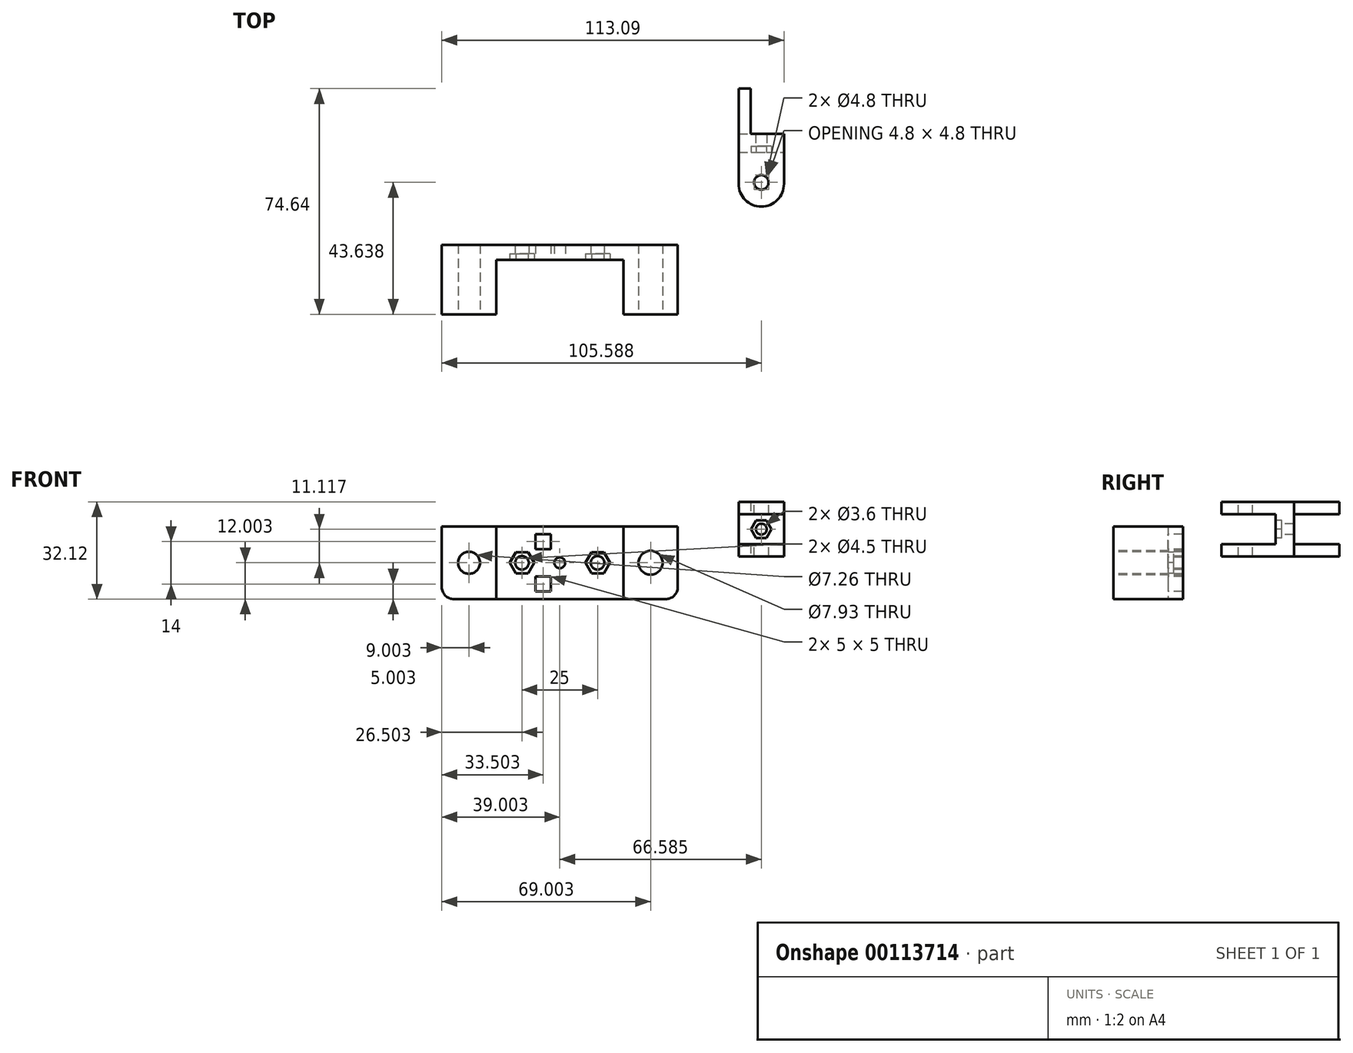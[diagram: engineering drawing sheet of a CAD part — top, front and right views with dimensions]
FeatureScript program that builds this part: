
annotation { "Feature Type Name" : "Feature", "Feature Type Description" : "" }
export const myFeature = defineFeature(function(context is Context, id is Id, definition is map)
    precondition{}
    {
        {
            var Q0;
            Q0=qCreatedBy(makeId("Front.planeOp"),FACE);
            var sketch = newSketch(context, id + "F0", { "sketchPlane" : qUnion([Q0])});
            skLineSegment(sketch, "E0", {"start": v(-49.77, -14.12) * mm, "end": v(-49.77, 9.88) * mm});
            skLineSegment(sketch, "E1", {"start": v(28.23, 9.88) * mm, "end": v(28.23, -14.12) * mm});
            skLineSegment(sketch, "E2", {"start": v(28.23, -14.12) * mm, "end": v(-49.77, -14.12) * mm});
            skLineSegment(sketch, "E3", {"start": v(-49.77, 9.88) * mm, "end": v(28.23, 9.88) * mm});
            skSolve(sketch);
        }
        {
            var Q0;
            Q0=makeQuery(id+"F0.imprint","IMPRINT",FACE,{"disambiguationData":[TD([[makeQuery(id+"F0.imprint","IMPRINT",EDGE,{"derivedFrom":sQuery(id+"F0.wireOp",EDGE,"E0")}),-1.0]])]});
            extrude(context, id + "F1", {"entities" : qUnion([Q0]), "depth" : 5 * mm});
        }
        {
            var Q0;
            Q0=makeQuery(id+"F1.opExtrude","CAP_FACE",FACE,{"disambiguationData":[OSD([sQuery(id+"F0.wireOp",EDGE,"E0"),sQuery(id+"F0.wireOp",EDGE,"pnh9ggrm-5665-z1nB-cMV6-CIKma8F3alFQ"),sQuery(id+"F0.wireOp",EDGE,"BvfvvXhj-ewnM-89mg-FvGF-KvGd08tOQLcB"),sQuery(id+"F0.wireOp",EDGE,"7k9m0oyc-eC8G-DHzC-QoAq-Q04KNSwf5TuD"),sQuery(id+"F0.wireOp",EDGE,"E1"),sQuery(id+"F0.wireOp",EDGE,"E2")])],"isStart":false});
            var sketch = newSketch(context, id + "F2", { "sketchPlane" : qUnion([Q0])});
            skCircle(sketch, "E4", {"center": v(-23.27, -2.12) * mm, "radius": 2.25 * mm});
            skCircle(sketch, "E5", {"center": v(1.73, -2.12) * mm, "radius": 2.25 * mm});
            skLineSegment(sketch, "E6", {"start": v(-49.77, -2.12) * mm, "end": v(28.23, -2.12) * mm, "construction": true});
            skCircle(sketch, "E7.cCircle", {"center": v(-23.27, -2.12) * mm, "radius": 3.5 * mm, "construction": true});
            skLineSegment(sketch, "E7.0", {"start": v(-25.29, 1.38) * mm, "end": v(-21.25, 1.38) * mm});
            skLineSegment(sketch, "E7.1", {"start": v(-21.25, 1.38) * mm, "end": v(-19.23, -2.12) * mm});
            skLineSegment(sketch, "E7.2", {"start": v(-19.23, -2.12) * mm, "end": v(-21.25, -5.62) * mm});
            skLineSegment(sketch, "E7.3", {"start": v(-21.25, -5.62) * mm, "end": v(-25.29, -5.62) * mm});
            skLineSegment(sketch, "E7.4", {"start": v(-25.29, -5.62) * mm, "end": v(-27.3, -2.12) * mm});
            skLineSegment(sketch, "E7.5", {"start": v(-27.3, -2.12) * mm, "end": v(-25.29, 1.38) * mm});
            skPoint(sketch, "E7.0.midPoint", {"position": v(-23.27, 1.38) * mm});
            skCircle(sketch, "E8.cCircle", {"center": v(1.73, -2.12) * mm, "radius": 3.5 * mm, "construction": true});
            skLineSegment(sketch, "E8.0", {"start": v(-0.29, 1.38) * mm, "end": v(3.75, 1.38) * mm});
            skLineSegment(sketch, "E8.1", {"start": v(3.75, 1.38) * mm, "end": v(5.77, -2.12) * mm});
            skLineSegment(sketch, "E8.2", {"start": v(5.77, -2.12) * mm, "end": v(3.75, -5.62) * mm});
            skLineSegment(sketch, "E8.3", {"start": v(3.75, -5.62) * mm, "end": v(-0.29, -5.62) * mm});
            skLineSegment(sketch, "E8.4", {"start": v(-0.29, -5.62) * mm, "end": v(-2.3, -2.12) * mm});
            skLineSegment(sketch, "E8.5", {"start": v(-2.3, -2.12) * mm, "end": v(-0.29, 1.38) * mm});
            skPoint(sketch, "E8.0.midPoint", {"position": v(1.73, 1.38) * mm});
            skCircle(sketch, "E9", {"center": v(-10.77, -2.12) * mm, "radius": 1.8 * mm});
            skLineSegment(sketch, "E10", {"start": v(-10.77, 9.88) * mm, "end": v(-10.77, -14.12) * mm, "construction": true});
            skSolve(sketch);
        }
        {
            var Q0;
            Q0=makeQuery(id+"F2.imprint","IMPRINT",FACE,{"disambiguationData":[TD([[makeQuery(id+"F2.imprint","IMPRINT",EDGE,{"derivedFrom":sQuery(id+"F2.wireOp",EDGE,"E4")}),1.0]])]});
            var Q1;
            Q1=makeQuery(id+"F2.imprint","IMPRINT",FACE,{"disambiguationData":[TD([[makeQuery(id+"F2.imprint","IMPRINT",EDGE,{"derivedFrom":sQuery(id+"F2.wireOp",EDGE,"E5")}),1.0]])]});
            extrude(context, id + "F3", {"entities" : qUnion([Q0, Q1]), "operationType" : NewBodyOperationType.REMOVE, "oppositeDirection" : true, "depth" : 25 * mm});
        }
        {
            var Q0;
            Q0=makeQuery(id+"F2.imprint","IMPRINT",FACE,{"disambiguationData":[TD([[makeQuery(id+"F2.imprint","IMPRINT",EDGE,{"derivedFrom":sQuery(id+"F2.wireOp",EDGE,"E4")}),-1.0]])]});
            var Q1;
            Q1=makeQuery(id+"F2.imprint","IMPRINT",FACE,{"disambiguationData":[TD([[makeQuery(id+"F2.imprint","IMPRINT",EDGE,{"derivedFrom":sQuery(id+"F2.wireOp",EDGE,"E5")}),-1.0]])]});
            extrude(context, id + "F4", {"entities" : qUnion([Q0, Q1]), "operationType" : NewBodyOperationType.REMOVE, "oppositeDirection" : true, "depth" : 2 * mm});
        }
        {
            var Q0;
            Q0=makeQuery(id+"F2.imprint","IMPRINT",FACE,{"disambiguationData":[TD([[makeQuery(id+"F2.imprint","IMPRINT",EDGE,{"derivedFrom":sQuery(id+"F2.wireOp",EDGE,"E7.0")}),1.0]])]});
            var sketch = newSketch(context, id + "F5", { "sketchPlane" : qUnion([Q0])});
            skLineSegment(sketch, "E11.bottom", {"start": v(-18.77, -6.62) * mm, "end": v(-13.77, -6.62) * mm});
            skLineSegment(sketch, "E11.top", {"start": v(-18.77, -11.62) * mm, "end": v(-13.77, -11.62) * mm});
            skLineSegment(sketch, "E11.left", {"start": v(-18.77, -6.62) * mm, "end": v(-18.77, -11.62) * mm});
            skLineSegment(sketch, "E11.right", {"start": v(-13.77, -6.62) * mm, "end": v(-13.77, -11.62) * mm});
            skLineSegment(sketch, "E12.bottom", {"start": v(-18.77, 2.38) * mm, "end": v(-13.77, 2.38) * mm});
            skLineSegment(sketch, "E12.top", {"start": v(-18.77, 7.38) * mm, "end": v(-13.77, 7.38) * mm});
            skLineSegment(sketch, "E12.left", {"start": v(-18.77, 2.38) * mm, "end": v(-18.77, 7.38) * mm});
            skLineSegment(sketch, "E12.right", {"start": v(-13.77, 2.38) * mm, "end": v(-13.77, 7.38) * mm});
            skLineSegment(sketch, "E13", {"start": v(-10.77, -14.12) * mm, "end": v(-10.77, 9.88) * mm, "construction": true});
            skSolve(sketch);
        }
        {
            var Q0;
            Q0=makeQuery(id+"F5.imprint","IMPRINT",FACE,{"disambiguationData":[TD([[makeQuery(id+"F5.imprint","IMPRINT",EDGE,{"derivedFrom":sQuery(id+"F5.wireOp",EDGE,"E11.bottom")}),-1.0]])]});
            var Q1;
            Q1=makeQuery(id+"F5.imprint","IMPRINT",FACE,{"disambiguationData":[TD([[makeQuery(id+"F5.imprint","IMPRINT",EDGE,{"derivedFrom":sQuery(id+"F5.wireOp",EDGE,"E12.bottom")}),1.0]])]});
            extrude(context, id + "F6", {"entities" : qUnion([Q0, Q1]), "operationType" : NewBodyOperationType.REMOVE, "oppositeDirection" : true, "depth" : 25 * mm});
        }
        {
            var Q0;
            Q0=makeQuery(id+"F1.opExtrude","CAP_FACE",FACE,{"disambiguationData":[OSD([sQuery(id+"F0.wireOp",EDGE,"E0"),sQuery(id+"F0.wireOp",EDGE,"pnh9ggrm-5665-z1nB-cMV6-CIKma8F3alFQ"),sQuery(id+"F0.wireOp",EDGE,"BvfvvXhj-ewnM-89mg-FvGF-KvGd08tOQLcB"),sQuery(id+"F0.wireOp",EDGE,"7k9m0oyc-eC8G-DHzC-QoAq-Q04KNSwf5TuD"),sQuery(id+"F0.wireOp",EDGE,"E1"),sQuery(id+"F0.wireOp",EDGE,"E2")])],"isStart":false});
            var sketch = newSketch(context, id + "F7", { "sketchPlane" : qUnion([Q0])});
            skLineSegment(sketch, "E14.bottom", {"start": v(28.23, 9.88) * mm, "end": v(10.23, 9.88) * mm});
            skLineSegment(sketch, "E14.top", {"start": v(28.23, -14.12) * mm, "end": v(10.23, -14.12) * mm});
            skLineSegment(sketch, "E14.left", {"start": v(28.23, 9.88) * mm, "end": v(28.23, -14.12) * mm});
            skLineSegment(sketch, "E14.right", {"start": v(10.23, 9.88) * mm, "end": v(10.23, -14.12) * mm});
            skLineSegment(sketch, "E15.bottom", {"start": v(-49.77, 9.88) * mm, "end": v(-31.77, 9.88) * mm});
            skLineSegment(sketch, "E15.top", {"start": v(-49.77, -14.12) * mm, "end": v(-31.77, -14.12) * mm});
            skLineSegment(sketch, "E15.left", {"start": v(-49.77, 9.88) * mm, "end": v(-49.77, -14.12) * mm});
            skLineSegment(sketch, "E15.right", {"start": v(-31.77, 9.88) * mm, "end": v(-31.77, -14.12) * mm});
            skSolve(sketch);
        }
        {
            var Q0;
            Q0=makeQuery(id+"F7.imprint","IMPRINT",FACE,{"disambiguationData":[TD([[makeQuery(id+"F7.imprint","IMPRINT",EDGE,{"derivedFrom":sQuery(id+"F7.wireOp",EDGE,"E15.bottom")}),-1.0]])]});
            var Q1;
            Q1=makeQuery(id+"F7.imprint","IMPRINT",FACE,{"disambiguationData":[TD([[makeQuery(id+"F7.imprint","IMPRINT",EDGE,{"derivedFrom":sQuery(id+"F7.wireOp",EDGE,"E14.bottom")}),-1.0]])]});
            extrude(context, id + "F8", {"entities" : qUnion([Q0, Q1]), "operationType" : NewBodyOperationType.ADD, "depth" : 18 * mm});
        }
        {
            var Q0;
            Q0=makeQuery(id+"F2.imprint","IMPRINT",FACE,{"disambiguationData":[TD([[makeQuery(id+"F2.imprint","IMPRINT",EDGE,{"derivedFrom":sQuery(id+"F2.wireOp",EDGE,"E7.0")}),1.0]])]});
            var sketch = newSketch(context, id + "F9", { "sketchPlane" : qUnion([Q0])});
            skCircle(sketch, "E16", {"center": v(-40.77, -2.12) * mm, "radius": 3.63 * mm});
            skCircle(sketch, "E17", {"center": v(19.23, -2.12) * mm, "radius": 3.96 * mm});
            skLineSegment(sketch, "E18", {"start": v(-49.77, -2.12) * mm, "end": v(28.23, -2.12) * mm, "construction": true});
            skSolve(sketch);
        }
        {
            var Q0;
            Q0=makeQuery(id+"F9.imprint","IMPRINT",FACE,{"disambiguationData":[TD([[makeQuery(id+"F9.imprint","IMPRINT",EDGE,{"derivedFrom":sQuery(id+"F9.wireOp",EDGE,"E16")}),1.0]])]});
            var Q1;
            Q1=makeQuery(id+"F9.imprint","IMPRINT",FACE,{"disambiguationData":[TD([[makeQuery(id+"F9.imprint","IMPRINT",EDGE,{"derivedFrom":sQuery(id+"F9.wireOp",EDGE,"E17")}),1.0]])]});
            extrude(context, id + "F10", {"entities" : qUnion([Q0, Q1]), "operationType" : NewBodyOperationType.REMOVE, "endBound" : BoundingType.SYMMETRIC, "oppositeDirection" : true, "depth" : 60 * mm});
        }
        {
            var Q0;
            Q0=makeQuery(id+"F8.boolean.opBoolean","MERGE",EDGE,{"derivedFrom":[makeQuery(id+"F1.opExtrude","SWEPT_EDGE",EDGE,{"disambiguationData":[OSD([sQuery(id+"F0.wireOp",EDGE,"E0"),sQuery(id+"F0.wireOp",EDGE,"E2")])]}),makeQuery(id+"F8.opExtrude","SWEPT_EDGE",EDGE,{"disambiguationData":[OSD([sQuery(id+"F7.wireOp",EDGE,"7sFVJVFp-NuRY-99qe-KacD-1ADUzF3ini2G.top"),sQuery(id+"F7.wireOp",EDGE,"7sFVJVFp-NuRY-99qe-KacD-1ADUzF3ini2G.left")])]})]});
            var Q1;
            Q1=makeQuery(id+"F8.boolean.opBoolean","MERGE",EDGE,{"derivedFrom":[makeQuery(id+"F1.opExtrude","SWEPT_EDGE",EDGE,{"disambiguationData":[OSD([sQuery(id+"F0.wireOp",EDGE,"E1"),sQuery(id+"F0.wireOp",EDGE,"E2")])]}),makeQuery(id+"F8.opExtrude","SWEPT_EDGE",EDGE,{"disambiguationData":[OSD([sQuery(id+"F7.wireOp",EDGE,"E14.top"),sQuery(id+"F7.wireOp",EDGE,"E14.left")])]})]});
            fillet(context, id + "F11", {"entities" : qUnion([Q0, Q1]), "radius" : 4 * mm, "tangentPropagation" : true, "allowEdgeOverflow" : false});
        }
        {
            var Q0;
            Q0=makeQuery(id+"F2.imprint","IMPRINT",FACE,{"disambiguationData":[TD([[makeQuery(id+"F2.imprint","IMPRINT",EDGE,{"derivedFrom":sQuery(id+"F2.wireOp",EDGE,"E9")}),1.0]])]});
            extrude(context, id + "F12", {"entities" : qUnion([Q0]), "operationType" : NewBodyOperationType.REMOVE, "oppositeDirection" : true, "depth" : 25 * mm});
        }
        {
            var Q0;
            Q0=qCreatedBy(makeId("Top.planeOp"),FACE);
            var sketch = newSketch(context, id + "F13", { "sketchPlane" : qUnion([Q0])});
            skLineSegment(sketch, "E19", {"start": v(48.32, 51.64) * mm, "end": v(52.32, 51.64) * mm});
            skLineSegment(sketch, "E20", {"start": v(52.32, 51.64) * mm, "end": v(52.32, 36.64) * mm});
            skLineSegment(sketch, "E21", {"start": v(52.32, 36.64) * mm, "end": v(63.32, 36.64) * mm});
            skLineSegment(sketch, "E22", {"start": v(63.32, 36.64) * mm, "end": v(63.32, 12.64) * mm});
            skLineSegment(sketch, "E23", {"start": v(63.32, 12.64) * mm, "end": v(48.32, 12.64) * mm});
            skLineSegment(sketch, "E24", {"start": v(48.32, 12.64) * mm, "end": v(48.32, 51.64) * mm});
            skSolve(sketch);
        }
        {
            var Q0;
            Q0=makeQuery(id+"F13.imprint","IMPRINT",FACE,{"disambiguationData":[TD([[makeQuery(id+"F13.imprint","IMPRINT",EDGE,{"derivedFrom":sQuery(id+"F13.wireOp",EDGE,"E19")}),-1.0]])]});
            extrude(context, id + "F14", {"entities" : qUnion([Q0]), "depth" : 18 * mm});
        }
        {
            var Q0;
            Q0=makeQuery(id+"F14.opExtrude","SWEPT_FACE",FACE,{"disambiguationData":[OSD([sQuery(id+"F13.wireOp",EDGE,"E20")])]});
            var sketch = newSketch(context, id + "F15", { "sketchPlane" : qUnion([Q0])});
            skLineSegment(sketch, "E25.bottom", {"start": v(51.64, 14) * mm, "end": v(36.64, 14) * mm});
            skLineSegment(sketch, "E25.top", {"start": v(51.64, 4) * mm, "end": v(36.64, 4) * mm});
            skLineSegment(sketch, "E25.left", {"start": v(51.64, 14) * mm, "end": v(51.64, 4) * mm});
            skLineSegment(sketch, "E25.right", {"start": v(36.64, 14) * mm, "end": v(36.64, 4) * mm});
            skSolve(sketch);
        }
        {
            var Q0;
            Q0=makeQuery(id+"F15.imprint","IMPRINT",FACE,{"disambiguationData":[TD([[makeQuery(id+"F15.imprint","IMPRINT",EDGE,{"derivedFrom":sQuery(id+"F15.wireOp",EDGE,"E25.bottom")}),1.0]])]});
            extrude(context, id + "F16", {"entities" : qUnion([Q0]), "operationType" : NewBodyOperationType.REMOVE, "oppositeDirection" : true, "depth" : 25 * mm});
        }
        {
            var Q0;
            Q0=makeQuery(id+"F14.opExtrude","SWEPT_FACE",FACE,{"disambiguationData":[OSD([sQuery(id+"F13.wireOp",EDGE,"E22")])]});
            var sketch = newSketch(context, id + "F17", { "sketchPlane" : qUnion([Q0])});
            skLineSegment(sketch, "E26.bottom", {"start": v(12.64, 14) * mm, "end": v(30.64, 14) * mm});
            skLineSegment(sketch, "E26.top", {"start": v(12.64, 4) * mm, "end": v(30.64, 4) * mm});
            skLineSegment(sketch, "E26.left", {"start": v(12.64, 14) * mm, "end": v(12.64, 4) * mm});
            skLineSegment(sketch, "E26.right", {"start": v(30.64, 14) * mm, "end": v(30.64, 4) * mm});
            skSolve(sketch);
        }
        {
            var Q0;
            Q0=makeQuery(id+"F17.imprint","IMPRINT",FACE,{"disambiguationData":[TD([[makeQuery(id+"F17.imprint","IMPRINT",EDGE,{"derivedFrom":sQuery(id+"F17.wireOp",EDGE,"E26.bottom")}),-1.0]])]});
            extrude(context, id + "F18", {"entities" : qUnion([Q0]), "operationType" : NewBodyOperationType.REMOVE, "oppositeDirection" : true, "depth" : 25 * mm});
        }
        {
            var Q0;
            Q0=makeQuery(id+"F14.opExtrude","CAP_FACE",FACE,{"disambiguationData":[OSD([sQuery(id+"F13.wireOp",EDGE,"E19"),sQuery(id+"F13.wireOp",EDGE,"E20"),sQuery(id+"F13.wireOp",EDGE,"E21"),sQuery(id+"F13.wireOp",EDGE,"E22"),sQuery(id+"F13.wireOp",EDGE,"E23"),sQuery(id+"F13.wireOp",EDGE,"E24")])],"isStart":false});
            var sketch = newSketch(context, id + "F19", { "sketchPlane" : qUnion([Q0])});
            skCircle(sketch, "E27", {"center": v(55.82, 20.64) * mm, "radius": 2.4 * mm});
            skSolve(sketch);
        }
        {
            var Q0;
            Q0=makeQuery(id+"F19.imprint","IMPRINT",FACE,{"disambiguationData":[TD([[makeQuery(id+"F19.imprint","IMPRINT",EDGE,{"derivedFrom":sQuery(id+"F19.wireOp",EDGE,"E27")}),1.0]])]});
            extrude(context, id + "F20", {"entities" : qUnion([Q0]), "operationType" : NewBodyOperationType.REMOVE, "oppositeDirection" : true, "depth" : 25 * mm});
        }
        {
            var Q0;
            {var subQ0=sQuery(id+"F13.wireOp",EDGE,"E24");var subQ1=sQuery(id+"F13.wireOp",EDGE,"E23");Q0=makeQuery(id+"F18.boolean.opBoolean","SPLIT",EDGE,{"disambiguationData":[TD([makeQuery(id+"F18.opExtrude","SWEPT_FACE",FACE,{"disambiguationData":[OSD([sQuery(id+"F17.wireOp",EDGE,"E26.bottom")])]})])],"derivedFrom":makeQuery(id+"F14.opExtrude","SWEPT_EDGE",EDGE,{"disambiguationData":[OSD([subQ1,subQ0])]})});}
            var Q1;
            {var subQ0=sQuery(id+"F13.wireOp",EDGE,"E24");var subQ1=sQuery(id+"F13.wireOp",EDGE,"E23");Q1=makeQuery(id+"F18.boolean.opBoolean","SPLIT",EDGE,{"disambiguationData":[TD([makeQuery(id+"F18.opExtrude","SWEPT_FACE",FACE,{"disambiguationData":[OSD([sQuery(id+"F17.wireOp",EDGE,"E26.top")])]})])],"derivedFrom":makeQuery(id+"F14.opExtrude","SWEPT_EDGE",EDGE,{"disambiguationData":[OSD([subQ1,subQ0])]})});}
            var Q2;
            {var subQ0=sQuery(id+"F13.wireOp",EDGE,"E23");var subQ1=sQuery(id+"F13.wireOp",EDGE,"E22");Q2=makeQuery(id+"F18.boolean.opBoolean","SPLIT",EDGE,{"disambiguationData":[TD([makeQuery(id+"F18.opExtrude","SWEPT_FACE",FACE,{"disambiguationData":[OSD([sQuery(id+"F17.wireOp",EDGE,"E26.top")])]})])],"derivedFrom":makeQuery(id+"F14.opExtrude","SWEPT_EDGE",EDGE,{"disambiguationData":[OSD([subQ1,subQ0])]})});}
            var Q3;
            {var subQ0=sQuery(id+"F13.wireOp",EDGE,"E23");var subQ1=sQuery(id+"F13.wireOp",EDGE,"E22");Q3=makeQuery(id+"F18.boolean.opBoolean","SPLIT",EDGE,{"disambiguationData":[TD([makeQuery(id+"F18.opExtrude","SWEPT_FACE",FACE,{"disambiguationData":[OSD([sQuery(id+"F17.wireOp",EDGE,"E26.bottom")])]})])],"derivedFrom":makeQuery(id+"F14.opExtrude","SWEPT_EDGE",EDGE,{"disambiguationData":[OSD([subQ1,subQ0])]})});}
            fillet(context, id + "F21", {"entities" : qUnion([Q0, Q1, Q2, Q3]), "radius" : 7.5 * mm, "tangentPropagation" : true, "allowEdgeOverflow" : false});
        }
        {
            var Q0;
            Q0=makeQuery(id+"F18.boolean.opBoolean","COPY",FACE,{"derivedFrom":makeQuery(id+"F18.opExtrude","SWEPT_FACE",FACE,{"disambiguationData":[OSD([sQuery(id+"F17.wireOp",EDGE,"E26.right")])]})});
            var sketch = newSketch(context, id + "F22", { "sketchPlane" : qUnion([Q0])});
            skLineSegment(sketch, "E28", {"start": v(48.32, 9) * mm, "end": v(63.32, 9) * mm, "construction": true});
            skPoint(sketch, "E29.cCircle.perimeterSnap0", {"position": v(55.82, 14) * mm});
            skPoint(sketch, "E29.0.midPoint.positionSnap0", {"position": v(55.82, 14) * mm});
            skCircle(sketch, "E30", {"center": v(55.82, 9) * mm, "radius": 1.8 * mm});
            skCircle(sketch, "E31.cCircle", {"center": v(55.82, 9) * mm, "radius": 2.9 * mm, "construction": true});
            skLineSegment(sketch, "E31.0", {"start": v(54.14, 11.9) * mm, "end": v(57.5, 11.9) * mm});
            skLineSegment(sketch, "E31.1", {"start": v(57.5, 11.9) * mm, "end": v(59.17, 9) * mm});
            skLineSegment(sketch, "E31.2", {"start": v(59.17, 9) * mm, "end": v(57.5, 6.1) * mm});
            skLineSegment(sketch, "E31.3", {"start": v(57.5, 6.1) * mm, "end": v(54.14, 6.1) * mm});
            skLineSegment(sketch, "E31.4", {"start": v(54.14, 6.1) * mm, "end": v(52.47, 9) * mm});
            skLineSegment(sketch, "E31.5", {"start": v(52.47, 9) * mm, "end": v(54.14, 11.9) * mm});
            skPoint(sketch, "E31.0.midPoint", {"position": v(55.82, 11.9) * mm});
            skSolve(sketch);
        }
        {
            var Q0;
            Q0=makeQuery(id+"F22.imprint","IMPRINT",FACE,{"disambiguationData":[TD([[makeQuery(id+"F22.imprint","IMPRINT",EDGE,{"derivedFrom":sQuery(id+"F22.wireOp",EDGE,"E30")}),1.0]])]});
            extrude(context, id + "F23", {"entities" : qUnion([Q0]), "operationType" : NewBodyOperationType.REMOVE, "oppositeDirection" : true, "depth" : 25 * mm});
        }
        {
            var Q0;
            Q0=makeQuery(id+"F22.imprint","IMPRINT",FACE,{"disambiguationData":[TD([[makeQuery(id+"F22.imprint","IMPRINT",EDGE,{"derivedFrom":sQuery(id+"F22.wireOp",EDGE,"E30")}),-1.0]])]});
            extrude(context, id + "F24", {"entities" : qUnion([Q0]), "operationType" : NewBodyOperationType.REMOVE, "oppositeDirection" : true, "depth" : 2 * mm});
        }
    });
